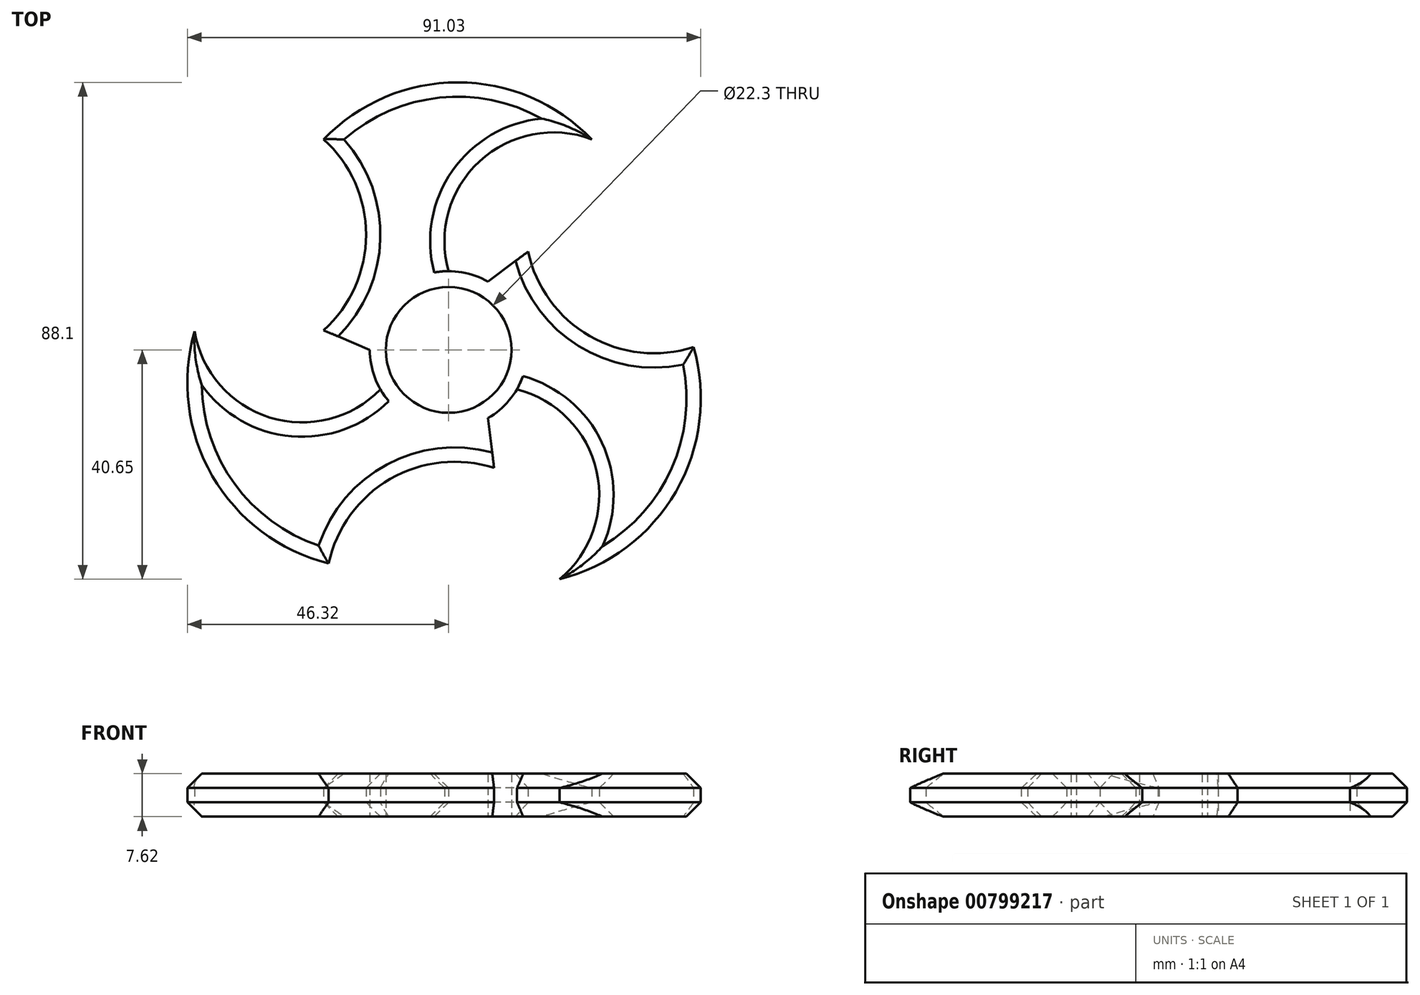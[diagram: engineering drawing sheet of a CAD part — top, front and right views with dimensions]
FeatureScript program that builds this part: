
annotation { "Feature Type Name" : "Feature", "Feature Type Description" : "" }
export const myFeature = defineFeature(function(context is Context, id is Id, definition is map)
    precondition{}
    {
        {
            var Q0;
            Q0=qCreatedBy(makeId("Top.planeOp"),FACE);
            var sketch = newSketch(context, id + "F0", { "sketchPlane" : qUnion([Q0])});
            skCircle(sketch, "E0", {"center": v(0, 0) * mm, "radius": 11.15 * mm});
            skCircle(sketch, "E1", {"center": v(0, 0) * mm, "radius": 13.97 * mm});
            skLineSegment(sketch, "E2", {"start": v(-13.97, 0) * mm, "end": v(-22.15, 3.48) * mm});
            skArc(sketch, "E3", {"start": v(-22.15, 3.48) * mm, "mid": v(-14.64, 20.42) * mm, "end": v(-22.15, 37.36) * mm});
            skArc(sketch, "E4", {"start": v(25.38, 37.36) * mm, "mid": v(1.61, 47.45) * mm, "end": v(-22.15, 37.36) * mm});
            skArc(sketch, "E5", {"start": v(25.38, 37.36) * mm, "mid": v(5.5, 33.47) * mm, "end": v(0, 13.97) * mm});
            skArc(sketch, "E6.1.0", {"start": v(8.06, -20.92) * mm, "mid": v(-10.36, -22.9) * mm, "end": v(-21.28, -37.86) * mm});
            skArc(sketch, "E6.1.1", {"start": v(-45.04, 3.3) * mm, "mid": v(-41.9, -22.33) * mm, "end": v(-21.28, -37.86) * mm});
            skLineSegment(sketch, "E6.1.2", {"start": v(6.98, -12.1) * mm, "end": v(8.06, -20.92) * mm});
            skArc(sketch, "E6.1.3", {"start": v(-45.04, 3.3) * mm, "mid": v(-31.73, -11.98) * mm, "end": v(-12.1, -6.98) * mm});
            skArc(sketch, "E6.2.0", {"start": v(14.1, 17.44) * mm, "mid": v(25, 2.47) * mm, "end": v(43.43, 0.5) * mm});
            skArc(sketch, "E6.2.1", {"start": v(19.66, -40.65) * mm, "mid": v(40.29, -25.12) * mm, "end": v(43.43, 0.5) * mm});
            skLineSegment(sketch, "E6.2.2", {"start": v(6.99, 12.1) * mm, "end": v(14.1, 17.44) * mm});
            skArc(sketch, "E6.2.3", {"start": v(19.66, -40.65) * mm, "mid": v(26.24, -21.5) * mm, "end": v(12.1, -6.99) * mm});
            skSolve(sketch);
        }
        {
            var Q0;
            {var subQ0=sQuery(id+"F0.wireOp",EDGE,"E2");Q0=makeQuery(id+"F0.imprint","IMPRINT",FACE,{"disambiguationData":[TD([[makeQuery(id+"F0.imprint","IMPRINT",EDGE,{"derivedFrom":subQ0}),-1.0]])]});}
            var Q1;
            Q1=makeQuery(id+"F0.imprint","IMPRINT",FACE,{"disambiguationData":[TD([[makeQuery(id+"F0.imprint","IMPRINT",EDGE,{"derivedFrom":sQuery(id+"F0.wireOp",EDGE,"E6.2.0")}),-1.0]])]});
            var Q2;
            Q2=makeQuery(id+"F0.imprint","IMPRINT",FACE,{"disambiguationData":[TD([[makeQuery(id+"F0.imprint","IMPRINT",EDGE,{"derivedFrom":sQuery(id+"F0.wireOp",EDGE,"E0")}),-1.0]])]});
            var Q3;
            Q3=makeQuery(id+"F0.imprint","IMPRINT",FACE,{"disambiguationData":[TD([[makeQuery(id+"F0.imprint","IMPRINT",EDGE,{"derivedFrom":sQuery(id+"F0.wireOp",EDGE,"E6.1.0")}),-1.0]])]});
            extrude(context, id + "F1", {"entities" : qUnion([Q0, Q1, Q2, Q3]), "depth" : 7.62 * mm, "offsetDistance" : 25.4 * mm});
        }
        {
            var Q0;
            Q0=makeQuery(id+"F1.opExtrude","CAP_EDGE",EDGE,{"disambiguationData":[OSD([sQuery(id+"F0.wireOp",EDGE,"E4")])],"isStart":true});
            var Q1;
            Q1=makeQuery(id+"F1.opExtrude","CAP_EDGE",EDGE,{"disambiguationData":[OSD([sQuery(id+"F0.wireOp",EDGE,"E6.2.1")])],"isStart":true});
            var Q2;
            Q2=makeQuery(id+"F1.opExtrude","CAP_EDGE",EDGE,{"disambiguationData":[OSD([sQuery(id+"F0.wireOp",EDGE,"E6.1.1")])],"isStart":true});
            var Q3;
            Q3=makeQuery(id+"F1.opExtrude","CAP_EDGE",EDGE,{"disambiguationData":[OSD([sQuery(id+"F0.wireOp",EDGE,"E6.1.1")])],"isStart":false});
            var Q4;
            Q4=makeQuery(id+"F1.opExtrude","CAP_EDGE",EDGE,{"disambiguationData":[OSD([sQuery(id+"F0.wireOp",EDGE,"E4")])],"isStart":false});
            var Q5;
            Q5=makeQuery(id+"F1.opExtrude","CAP_EDGE",EDGE,{"disambiguationData":[OSD([sQuery(id+"F0.wireOp",EDGE,"E6.2.1")])],"isStart":false});
            var Q6;
            Q6=makeQuery(id+"F1.opExtrude","CAP_EDGE",EDGE,{"disambiguationData":[OSD([sQuery(id+"F0.wireOp",EDGE,"E3")])],"isStart":false});
            var Q7;
            Q7=makeQuery(id+"F1.opExtrude","CAP_EDGE",EDGE,{"disambiguationData":[OSD([sQuery(id+"F0.wireOp",EDGE,"E5")])],"isStart":false});
            var Q8;
            Q8=makeQuery(id+"F1.opExtrude","CAP_EDGE",EDGE,{"disambiguationData":[OSD([sQuery(id+"F0.wireOp",EDGE,"E6.2.3")])],"isStart":false});
            var Q9;
            Q9=makeQuery(id+"F1.opExtrude","CAP_EDGE",EDGE,{"disambiguationData":[OSD([sQuery(id+"F0.wireOp",EDGE,"E6.2.0")])],"isStart":false});
            var Q10;
            Q10=makeQuery(id+"F1.opExtrude","CAP_EDGE",EDGE,{"disambiguationData":[OSD([sQuery(id+"F0.wireOp",EDGE,"E6.1.0")])],"isStart":false});
            var Q11;
            Q11=makeQuery(id+"F1.opExtrude","CAP_EDGE",EDGE,{"disambiguationData":[OSD([sQuery(id+"F0.wireOp",EDGE,"E6.1.3")])],"isStart":false});
            var Q12;
            Q12=makeQuery(id+"F1.opExtrude","CAP_EDGE",EDGE,{"disambiguationData":[OSD([sQuery(id+"F0.wireOp",EDGE,"E6.1.3")])],"isStart":true});
            var Q13;
            Q13=makeQuery(id+"F1.opExtrude","CAP_EDGE",EDGE,{"disambiguationData":[OSD([sQuery(id+"F0.wireOp",EDGE,"E3")])],"isStart":true});
            var Q14;
            Q14=makeQuery(id+"F1.opExtrude","CAP_EDGE",EDGE,{"disambiguationData":[OSD([sQuery(id+"F0.wireOp",EDGE,"E6.2.0")])],"isStart":true});
            var Q15;
            Q15=makeQuery(id+"F1.opExtrude","CAP_EDGE",EDGE,{"disambiguationData":[OSD([sQuery(id+"F0.wireOp",EDGE,"E6.2.3")])],"isStart":true});
            var Q16;
            Q16=makeQuery(id+"F1.opExtrude","CAP_EDGE",EDGE,{"disambiguationData":[OSD([sQuery(id+"F0.wireOp",EDGE,"E6.1.0")])],"isStart":true});
            var Q17;
            Q17=makeQuery(id+"F1.opExtrude","CAP_EDGE",EDGE,{"disambiguationData":[OSD([sQuery(id+"F0.wireOp",EDGE,"E5")])],"isStart":true});
            chamfer(context, id + "F2", {"entities" : qUnion([Q0, Q1, Q2, Q3, Q4, Q5, Q6, Q7, Q8, Q9, Q10, Q11, Q12, Q13, Q14, Q15, Q16, Q17]), "width" : 2.54 * mm, "tangentPropagation" : true});
        }
    });
